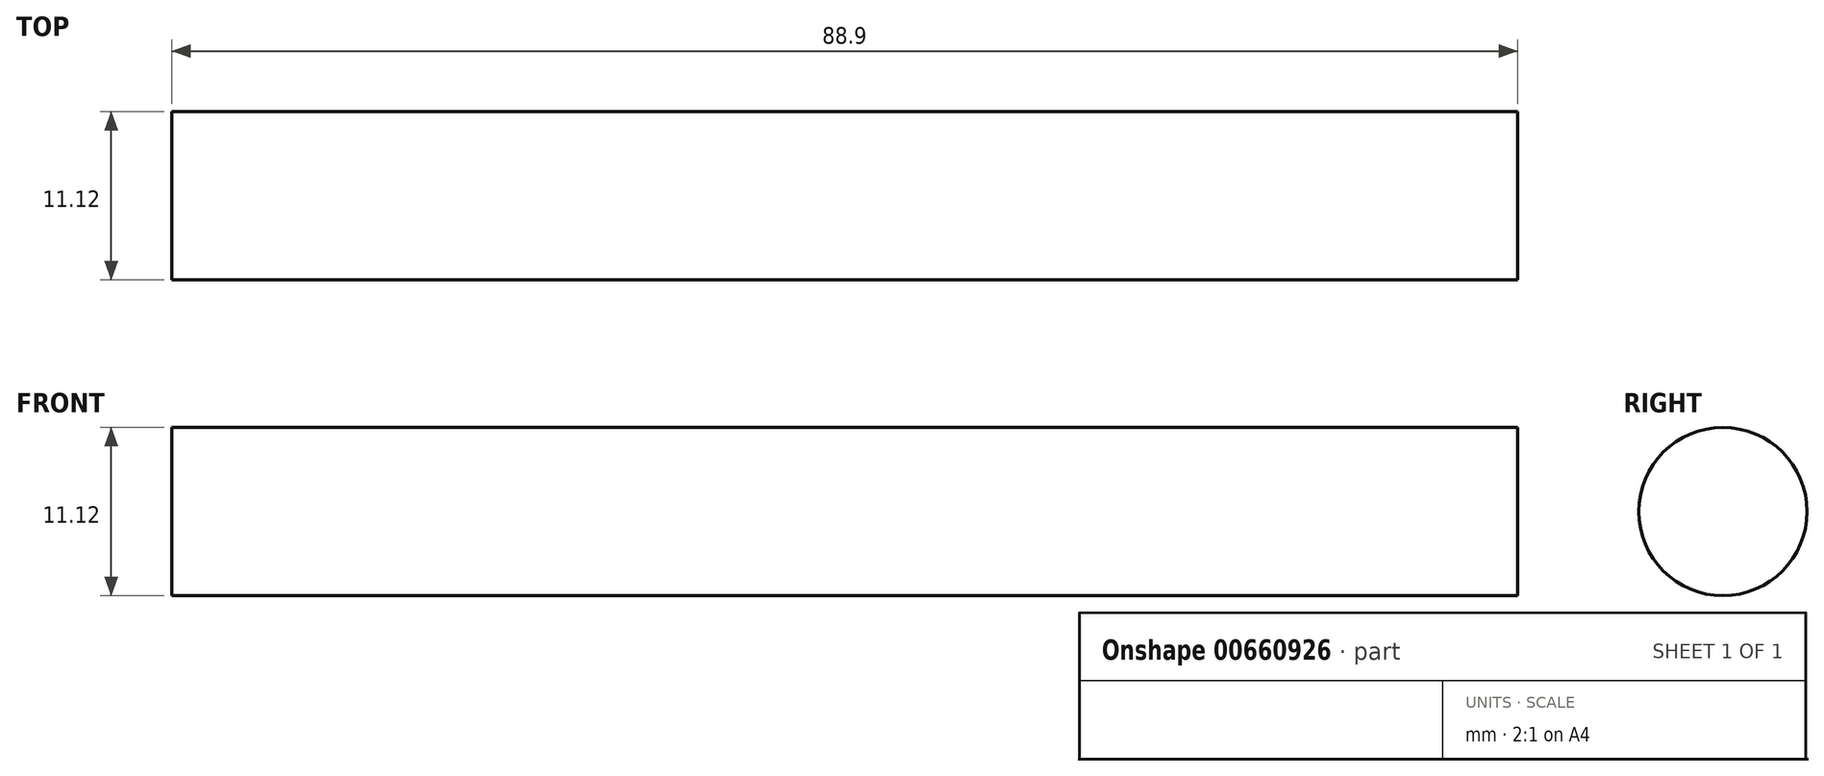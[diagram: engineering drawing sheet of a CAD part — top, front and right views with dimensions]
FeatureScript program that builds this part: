
annotation { "Feature Type Name" : "Feature", "Feature Type Description" : "" }
export const myFeature = defineFeature(function(context is Context, id is Id, definition is map)
    precondition{}
    {
        {
            var Q0;
            Q0=qCreatedBy(makeId("Front.planeOp"),FACE);
            var sketch = newSketch(context, id + "F0", { "sketchPlane" : qUnion([Q0])});
            skLineSegment(sketch, "E0", {"start": v(0, 0) * mm, "end": v(70, 0) * mm, "construction": true});
            skLineSegment(sketch, "E1.bottom", {"start": v(0, 0) * mm, "end": v(101.6, 0) * mm});
            skLineSegment(sketch, "E1.top", {"start": v(0, 12.7) * mm, "end": v(101.6, 12.7) * mm});
            skLineSegment(sketch, "E1.left", {"start": v(0, 0) * mm, "end": v(0, 12.7) * mm});
            skLineSegment(sketch, "E1.right", {"start": v(101.6, 0) * mm, "end": v(101.6, 12.7) * mm});
            skLineSegment(sketch, "E2", {"start": v(92.08, 12.7) * mm, "end": v(92.08, 9.52) * mm});
            skLineSegment(sketch, "E3", {"start": v(92.08, 9.52) * mm, "end": v(50.8, 12.7) * mm});
            skLineSegment(sketch, "E4", {"start": v(50.8, 12.7) * mm, "end": v(19.05, 12.7) * mm});
            skLineSegment(sketch, "E5", {"start": v(19.05, 12.7) * mm, "end": v(0, 9.52) * mm});
            skLineSegment(sketch, "E6", {"start": v(92.08, 12.7) * mm, "end": v(101.6, 12.7) * mm});
            skLineSegment(sketch, "E7.bottom", {"start": v(101.6, 0) * mm, "end": v(12.7, 0) * mm});
            skLineSegment(sketch, "E7.top", {"start": v(101.6, 5.56) * mm, "end": v(12.7, 5.56) * mm});
            skLineSegment(sketch, "E7.left", {"start": v(101.6, 0) * mm, "end": v(101.6, 5.56) * mm});
            skLineSegment(sketch, "E7.right", {"start": v(12.7, 0) * mm, "end": v(12.7, 5.56) * mm});
            skLineSegment(sketch, "E8.bottom", {"start": v(12.7, 0) * mm, "end": v(0, 0) * mm});
            skLineSegment(sketch, "E8.top", {"start": v(12.7, 8.9) * mm, "end": v(0, 8.9) * mm});
            skLineSegment(sketch, "E8.left", {"start": v(12.7, 0) * mm, "end": v(12.7, 8.9) * mm});
            skLineSegment(sketch, "E8.right", {"start": v(0, 0) * mm, "end": v(0, 8.9) * mm});
            skSolve(sketch);
        }
        {
            var Q0;
            Q0=makeQuery(id+"F0.imprint","IMPRINT",FACE,{"disambiguationData":[TD([[makeQuery(id+"F0.imprint","IMPRINT",EDGE,{"derivedFrom":sQuery(id+"F0.wireOp",EDGE,"E1.right")}),1.0]])]});
            var Q1;
            Q1=sQuery(id+"F0.wireOp",EDGE,"gFEaQceJ-CucC-QKus-wjkh-rpYHdM7YVut3");
            var Q2;
            Q2=sQuery(id+"F0.wireOp",EDGE,"E5");
            var Q3;
            Q3=sQuery(id+"F0.wireOp",EDGE,"E4");
            var Q4;
            Q4=sQuery(id+"F0.wireOp",EDGE,"E3");
            var Q5;
            Q5=sQuery(id+"F0.wireOp",EDGE,"E2");
            var Q6;
            Q6=sQuery(id+"F0.wireOp",EDGE,"E1.right");
            var Q7;
            Q7=sQuery(id+"F0.wireOp",EDGE,"E6");
            var Q8;
            Q8=sQuery(id+"F0.wireOp",EDGE,"E0");
            revolve(context, id + "F1", {"entities" : qUnion([Q0]), "surfaceEntities" : qUnion([Q1, Q2, Q3, Q4, Q5, Q6, Q7]), "axis" : qUnion([Q8]), "revolveType" : RevolveType.FULL});
        }
    });
